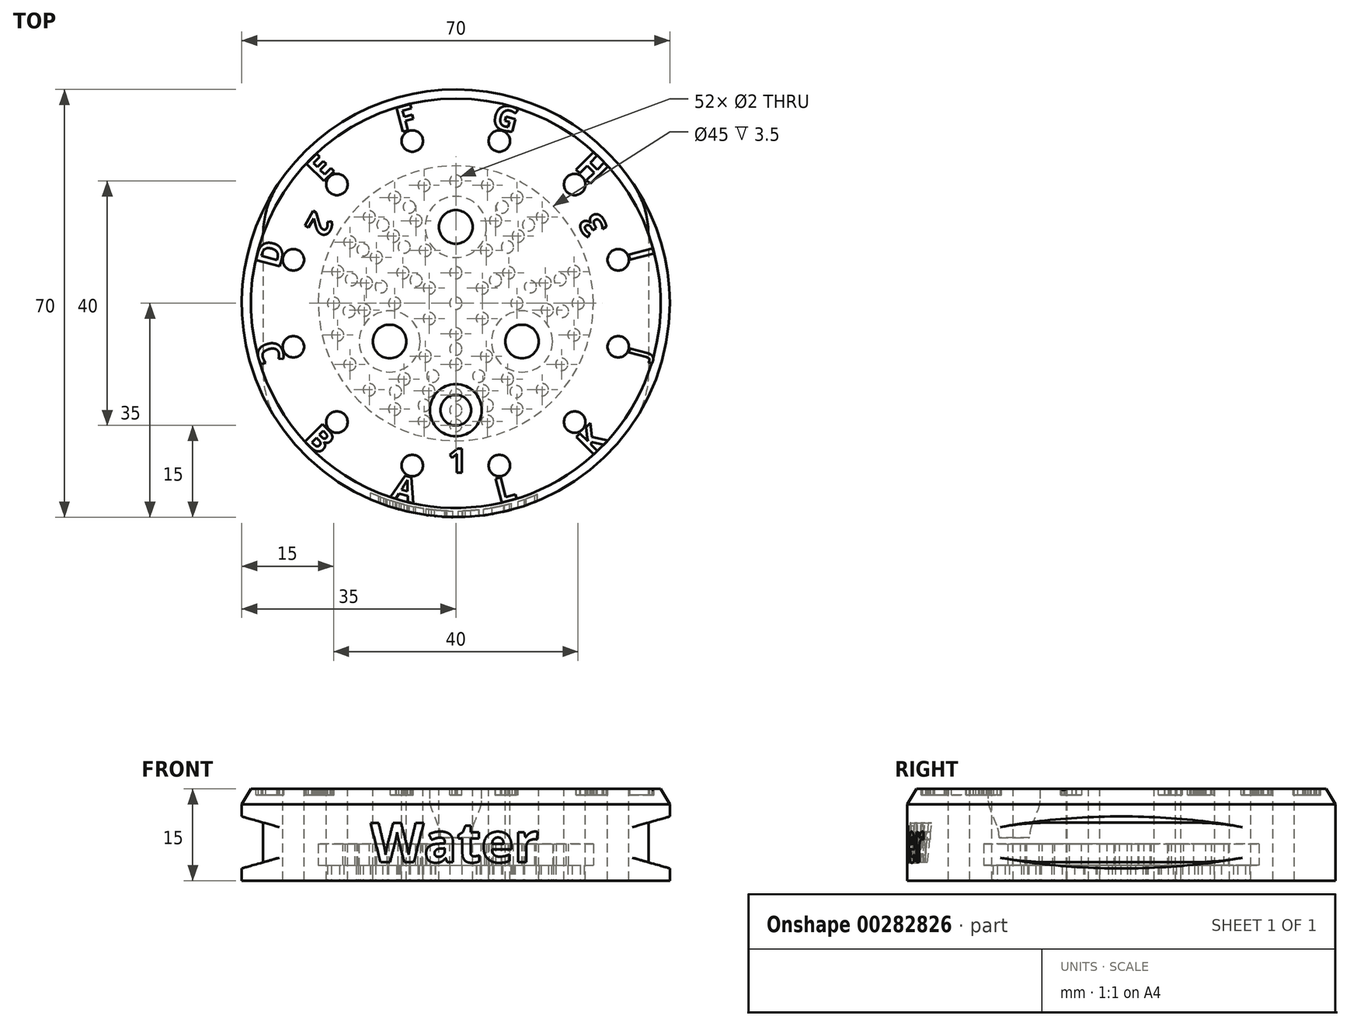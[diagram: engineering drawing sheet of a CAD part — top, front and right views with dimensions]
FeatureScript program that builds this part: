
annotation { "Feature Type Name" : "Feature", "Feature Type Description" : "" }
export const myFeature = defineFeature(function(context is Context, id is Id, definition is map)
    precondition{}
    {
        {
            var Q0;
            Q0=qCreatedBy(makeId("Top.planeOp"),FACE);
            var sketch = newSketch(context, id + "F0", { "sketchPlane" : qUnion([Q0])});
            skCircle(sketch, "E0", {"center": v(0, 0) * mm, "radius": 35 * mm});
            skSolve(sketch);
        }
        {
            var Q0;
            Q0=qSketchRegion(id+"F0",true);
            extrude(context, id + "F1", {"entities" : qUnion([Q0]), "depth" : 15 * mm});
        }
        {
            var Q0;
            Q0=qCreatedBy(makeId("Front.planeOp"),FACE);
            var sketch = newSketch(context, id + "F2", { "sketchPlane" : qUnion([Q0])});
            skText(sketch, "E1", { "text": "Water", "fontName": "OpenSans-Bold.ttf"});
            const initialGuessF2  = {"E1": [-0.01396, 0.003, 1, 0, 0.0065]};
            skSetInitialGuess(sketch, initialGuessF2);
            skSolve(sketch);
        }
        {
            var Q0;
            Q0=qSketchRegion(id+"F2",true);
            var Q1;
            Q1=makeQuery(id+"F1.opExtrude","SWEPT_FACE",FACE,{"disambiguationData":[OSD([sQuery(id+"F0.wireOp",EDGE,"E0")])]});
            extrude(context, id + "F3", {"entities" : qUnion([Q0]), "operationType" : NewBodyOperationType.REMOVE, "endBound" : BoundingType.THROUGH_ALL, "endBoundEntityFace" : qUnion([Q1]), "depth" : 25 * mm});
        }
        {
            var Q0;
            Q0=makeQuery(id+"F1.opExtrude","CAP_FACE",FACE,{"disambiguationData":[OSD([sQuery(id+"F0.wireOp",EDGE,"E0")])],"isStart":false});
            var sketch = newSketch(context, id + "F4", { "sketchPlane" : qUnion([Q0])});
            skCircle(sketch, "E2", {"center": v(0, 0) * mm, "radius": 34 * mm});
            skSolve(sketch);
        }
        {
            var Q0;
            Q0=qSketchRegion(id+"F4",true);
            var Q1;
            Q1=makeQuery(id+"F1.opExtrude","CAP_FACE",FACE,{"disambiguationData":[OSD([sQuery(id+"F0.wireOp",EDGE,"E0")])],"isStart":true});
            extrude(context, id + "F5", {"entities" : qUnion([Q0]), "operationType" : NewBodyOperationType.ADD, "endBound" : BoundingType.UP_TO_SURFACE, "oppositeDirection" : true, "endBoundEntityFace" : qUnion([Q1]), "depth" : 25 * mm});
        }
        {
            var Q0;
            Q0=qCreatedBy(makeId("Front.planeOp"),FACE);
            var sketch = newSketch(context, id + "F6", { "sketchPlane" : qUnion([Q0])});
            skLineSegment(sketch, "E3", {"start": v(-35, 10.5) * mm, "end": v(-35, 2) * mm});
            skLineSegment(sketch, "E4", {"start": v(-35, 2) * mm, "end": v(-31.5, 3) * mm});
            skLineSegment(sketch, "E5", {"start": v(-31.5, 3) * mm, "end": v(-31.5, 9.5) * mm});
            skLineSegment(sketch, "E6", {"start": v(-31.5, 9.5) * mm, "end": v(-35, 10.5) * mm});
            skLineSegment(sketch, "E7.MirrorCS", {"start": v(35, 10.5) * mm, "end": v(35, 2) * mm});
            skLineSegment(sketch, "E8.MirrorCS", {"start": v(31.5, 9.5) * mm, "end": v(35, 10.5) * mm});
            skLineSegment(sketch, "E9.MirrorCS", {"start": v(35, 2) * mm, "end": v(31.5, 3) * mm});
            skLineSegment(sketch, "E10.MirrorCS", {"start": v(31.5, 3) * mm, "end": v(31.5, 9.5) * mm});
            skSolve(sketch);
        }
        {
            var Q0;
            Q0=qSketchRegion(id+"F6",true);
            extrude(context, id + "F7", {"entities" : qUnion([Q0]), "operationType" : NewBodyOperationType.REMOVE, "endBound" : BoundingType.THROUGH_ALL, "oppositeDirection" : true, "depth" : 25 * mm, "hasSecondDirection" : true, "secondDirectionBound" : SecondDirectionBoundingType.THROUGH_ALL, "secondDirectionOppositeDirection" : false, "secondDirectionDepth" : 25 * mm});
        }
        {
            var Q0;
            {var subQ0=sQuery(id+"F0.wireOp",EDGE,"E0");Q0=makeQuery(id+"F7.boolean.opBoolean","INTERSECT",EDGE,{"disambiguationData":[OD(0.0)],"derivedFrom":[makeQuery(id+"F3.boolean.opBoolean","SPLIT",FACE,{"disambiguationData":[TD([makeQuery(id+"F1.opExtrude","CAP_FACE",FACE,{"disambiguationData":[OSD([subQ0])],"isStart":true})])],"derivedFrom":makeQuery(id+"F1.opExtrude","SWEPT_FACE",FACE,{"disambiguationData":[OSD([subQ0])]})}),makeQuery(id+"F7.opExtrude","SWEPT_FACE",FACE,{"disambiguationData":[OSD([sQuery(id+"F6.wireOp",EDGE,"E5")])]})]});}
            var Q1;
            {var subQ0=sQuery(id+"F0.wireOp",EDGE,"E0");Q1=makeQuery(id+"F7.boolean.opBoolean","INTERSECT",EDGE,{"disambiguationData":[OD(0.0)],"derivedFrom":[makeQuery(id+"F3.boolean.opBoolean","SPLIT",FACE,{"disambiguationData":[TD([makeQuery(id+"F1.opExtrude","CAP_FACE",FACE,{"disambiguationData":[OSD([subQ0])],"isStart":true})])],"derivedFrom":makeQuery(id+"F1.opExtrude","SWEPT_FACE",FACE,{"disambiguationData":[OSD([subQ0])]})}),makeQuery(id+"F7.opExtrude","SWEPT_FACE",FACE,{"disambiguationData":[OSD([sQuery(id+"F6.wireOp",EDGE,"E10.MirrorCS")])]})]});}
            var Q2;
            {var subQ0=sQuery(id+"F0.wireOp",EDGE,"E0");Q2=makeQuery(id+"F7.boolean.opBoolean","INTERSECT",EDGE,{"disambiguationData":[OD(1.0)],"derivedFrom":[makeQuery(id+"F3.boolean.opBoolean","SPLIT",FACE,{"disambiguationData":[TD([makeQuery(id+"F1.opExtrude","CAP_FACE",FACE,{"disambiguationData":[OSD([subQ0])],"isStart":true})])],"derivedFrom":makeQuery(id+"F1.opExtrude","SWEPT_FACE",FACE,{"disambiguationData":[OSD([subQ0])]})}),makeQuery(id+"F7.opExtrude","SWEPT_FACE",FACE,{"disambiguationData":[OSD([sQuery(id+"F6.wireOp",EDGE,"E10.MirrorCS")])]})]});}
            var Q3;
            {var subQ0=sQuery(id+"F0.wireOp",EDGE,"E0");Q3=makeQuery(id+"F7.boolean.opBoolean","INTERSECT",EDGE,{"disambiguationData":[OD(1.0)],"derivedFrom":[makeQuery(id+"F3.boolean.opBoolean","SPLIT",FACE,{"disambiguationData":[TD([makeQuery(id+"F1.opExtrude","CAP_FACE",FACE,{"disambiguationData":[OSD([subQ0])],"isStart":true})])],"derivedFrom":makeQuery(id+"F1.opExtrude","SWEPT_FACE",FACE,{"disambiguationData":[OSD([subQ0])]})}),makeQuery(id+"F7.opExtrude","SWEPT_FACE",FACE,{"disambiguationData":[OSD([sQuery(id+"F6.wireOp",EDGE,"E5")])]})]});}
            fillet(context, id + "F8", {"entities" : qUnion([Q0, Q1, Q2, Q3]), "radius" : 15 * mm, "tangentPropagation" : true, "allowEdgeOverflow" : false});
        }
        {
            var Q0;
            Q0=makeQuery(id+"F1.opExtrude","CAP_FACE",FACE,{"disambiguationData":[OSD([sQuery(id+"F0.wireOp",EDGE,"E0")])],"isStart":false});
            var sketch = newSketch(context, id + "F9", { "sketchPlane" : qUnion([Q0])});
            skCircle(sketch, "E11", {"center": v(0, 12.5) * mm, "radius": 2.75 * mm});
            skCircle(sketch, "E12.1.0", {"center": v(-10.83, -6.25) * mm, "radius": 2.75 * mm});
            skCircle(sketch, "E12.2.0", {"center": v(10.83, -6.25) * mm, "radius": 2.75 * mm});
            skPoint(sketch, "E12.center", {"position": v(0, 0) * mm});
            skCircle(sketch, "E13", {"center": v(0, 0) * mm, "radius": 12.5 * mm, "construction": true});
            skSolve(sketch);
        }
        {
            var Q0;
            Q0=qSketchRegion(id+"F9",true);
            extrude(context, id + "F10", {"entities" : qUnion([Q0]), "operationType" : NewBodyOperationType.REMOVE, "endBound" : BoundingType.THROUGH_ALL, "oppositeDirection" : true, "depth" : 25 * mm});
        }
        {
            var Q0;
            Q0=makeQuery(id+"F1.opExtrude","CAP_FACE",FACE,{"disambiguationData":[OSD([sQuery(id+"F0.wireOp",EDGE,"E0")])],"isStart":false});
            var sketch = newSketch(context, id + "F11", { "sketchPlane" : qUnion([Q0])});
            skCircle(sketch, "E14", {"center": v(0, -17.5) * mm, "radius": 2.5 * mm});
            skCircle(sketch, "E15", {"center": v(0, 0) * mm, "radius": 17.5 * mm, "construction": true});
            skSolve(sketch);
        }
        {
            var Q0;
            Q0=qSketchRegion(id+"F11",true);
            extrude(context, id + "F12", {"entities" : qUnion([Q0]), "operationType" : NewBodyOperationType.REMOVE, "endBound" : BoundingType.THROUGH_ALL, "oppositeDirection" : true, "depth" : 25 * mm});
        }
        {
            var Q0;
            Q0=makeQuery(id+"F1.opExtrude","CAP_FACE",FACE,{"disambiguationData":[OSD([sQuery(id+"F0.wireOp",EDGE,"E0")])],"isStart":false});
            var sketch = newSketch(context, id + "F13", { "sketchPlane" : qUnion([Q0])});
            skCircle(sketch, "E16", {"center": v(0, -17.5) * mm, "radius": 4.25 * mm});
            skSolve(sketch);
        }
        {
            var Q0;
            Q0=qSketchRegion(id+"F13",true);
            extrude(context, id + "F14", {"entities" : qUnion([Q0]), "operationType" : NewBodyOperationType.REMOVE, "oppositeDirection" : true, "depth" : 7.5 * mm});
        }
        {
            var Q0;
            Q0=makeQuery(id+"F14.boolean.opBoolean","COPY",EDGE,{"derivedFrom":makeQuery(id+"F14.opExtrude","CAP_EDGE",EDGE,{"disambiguationData":[OSD([sQuery(id+"F13.wireOp",EDGE,"E16")])],"isStart":false})});
            chamfer(context, id + "F15", {"entities" : qUnion([Q0]), "chamferType" : ChamferType.TWO_OFFSETS, "width1" : 5 * mm, "oppositeDirection" : true, "width2" : 2 * mm, "tangentPropagation" : true});
        }
        {
            var Q0;
            {var subQ0=sQuery(id+"F13.wireOp",EDGE,"E16");Q0=makeQuery(id+"F15.opChamfer","BLEND_EDGE",EDGE,{"blendedFrom":[makeQuery(id+"F14.boolean.opBoolean","COPY",EDGE,{"derivedFrom":makeQuery(id+"F14.opExtrude","CAP_EDGE",EDGE,{"disambiguationData":[OSD([subQ0])],"isStart":false})}),makeQuery(id+"F14.boolean.opBoolean","COPY",FACE,{"derivedFrom":makeQuery(id+"F14.opExtrude","SWEPT_FACE",FACE,{"disambiguationData":[OSD([subQ0])]})})],"blendedInto":[makeQuery(id+"F14.boolean.opBoolean","COPY",FACE,{"derivedFrom":makeQuery(id+"F14.opExtrude","SWEPT_FACE",FACE,{"disambiguationData":[OSD([subQ0])]})})]});}
            var Q1;
            Q1=makeQuery(id+"F15.opChamfer","BLEND_EDGE",EDGE,{"blendedFrom":[makeQuery(id+"F14.boolean.opBoolean","COPY",EDGE,{"derivedFrom":makeQuery(id+"F14.opExtrude","CAP_EDGE",EDGE,{"disambiguationData":[OSD([sQuery(id+"F13.wireOp",EDGE,"E16")])],"isStart":false})}),makeQuery(id+"F12.boolean.opBoolean","COPY",FACE,{"derivedFrom":makeQuery(id+"F12.opExtrude","SWEPT_FACE",FACE,{"disambiguationData":[OSD([sQuery(id+"F11.wireOp",EDGE,"E14")])]})})],"blendedInto":[makeQuery(id+"F12.boolean.opBoolean","COPY",FACE,{"derivedFrom":makeQuery(id+"F12.opExtrude","SWEPT_FACE",FACE,{"disambiguationData":[OSD([sQuery(id+"F11.wireOp",EDGE,"E14")])]})})]});
            fillet(context, id + "F16", {"entities" : qUnion([Q0, Q1]), "radius" : 5 * mm, "tangentPropagation" : true, "allowEdgeOverflow" : false});
        }
        {
            var Q0;
            Q0=makeQuery(id+"F1.opExtrude","CAP_FACE",FACE,{"disambiguationData":[OSD([sQuery(id+"F0.wireOp",EDGE,"E0")])],"isStart":false});
            var sketch = newSketch(context, id + "F17", { "sketchPlane" : qUnion([Q0])});
            skCircle(sketch, "E17", {"center": v(19.45, 19.45) * mm, "radius": 1.75 * mm});
            skCircle(sketch, "E18", {"center": v(0, 0) * mm, "radius": 27.5 * mm, "construction": true});
            skLineSegment(sketch, "E19", {"start": v(0, 0) * mm, "end": v(19.45, 19.45) * mm, "construction": true});
            skCircle(sketch, "E20.1.1", {"center": v(7.12, 26.56) * mm, "radius": 1.75 * mm});
            skCircle(sketch, "E20.2.1", {"center": v(-7.12, 26.56) * mm, "radius": 1.75 * mm});
            skCircle(sketch, "E20.3.1", {"center": v(-19.45, 19.45) * mm, "radius": 1.75 * mm});
            skCircle(sketch, "E20.4.1", {"center": v(-26.56, 7.12) * mm, "radius": 1.75 * mm});
            skCircle(sketch, "E20.5.1", {"center": v(-26.56, -7.12) * mm, "radius": 1.75 * mm});
            skCircle(sketch, "E20.6.1", {"center": v(-19.45, -19.45) * mm, "radius": 1.75 * mm});
            skCircle(sketch, "E20.7.1", {"center": v(-7.12, -26.56) * mm, "radius": 1.75 * mm});
            skCircle(sketch, "E20.8.1", {"center": v(7.12, -26.56) * mm, "radius": 1.75 * mm});
            skCircle(sketch, "E20.9.1", {"center": v(19.45, -19.45) * mm, "radius": 1.75 * mm});
            skCircle(sketch, "E20.10.1", {"center": v(26.56, -7.12) * mm, "radius": 1.75 * mm});
            skCircle(sketch, "E20.11.1", {"center": v(26.56, 7.12) * mm, "radius": 1.75 * mm});
            skSolve(sketch);
        }
        {
            var Q0;
            Q0=qSketchRegion(id+"F17",true);
            extrude(context, id + "F18", {"entities" : qUnion([Q0]), "operationType" : NewBodyOperationType.REMOVE, "endBound" : BoundingType.THROUGH_ALL, "oppositeDirection" : true, "depth" : 25 * mm});
        }
        {
            var Q0;
            Q0=makeQuery(id+"F1.opExtrude","CAP_EDGE",EDGE,{"disambiguationData":[OSD([sQuery(id+"F0.wireOp",EDGE,"E0")])],"isStart":false});
            chamfer(context, id + "F19", {"entities" : qUnion([Q0]), "chamferType" : ChamferType.TWO_OFFSETS, "width1" : 2.5 * mm, "oppositeDirection" : true, "width2" : 1.5 * mm, "tangentPropagation" : true});
        }
        {
            var Q0;
            Q0=makeQuery(id+"F1.opExtrude","CAP_FACE",FACE,{"disambiguationData":[OSD([sQuery(id+"F0.wireOp",EDGE,"E0")])],"isStart":false});
            var sketch = newSketch(context, id + "F20", { "sketchPlane" : qUnion([Q0])});
            skText(sketch, "E21", { "text": "A", "fontName": "OpenSans-Bold.ttf"});
            skText(sketch, "E22", { "text": "B", "fontName": "OpenSans-Bold.ttf"});
            skText(sketch, "E23", { "text": "C", "fontName": "OpenSans-Bold.ttf"});
            skText(sketch, "E24", { "text": "E", "fontName": "OpenSans-Bold.ttf"});
            skText(sketch, "E25", { "text": "F", "fontName": "OpenSans-Bold.ttf"});
            skText(sketch, "E26", { "text": "G", "fontName": "OpenSans-Bold.ttf"});
            skText(sketch, "E27", { "text": "H", "fontName": "OpenSans-Bold.ttf"});
            skText(sketch, "E28", { "text": "I", "fontName": "OpenSans-Bold.ttf"});
            skText(sketch, "E29", { "text": "J", "fontName": "OpenSans-Bold.ttf"});
            skText(sketch, "E30", { "text": "K", "fontName": "OpenSans-Bold.ttf"});
            skText(sketch, "E31", { "text": "L", "fontName": "OpenSans-Bold.ttf"});
            skText(sketch, "E32", { "text": "D", "fontName": "OpenSans-Bold.ttf"});
            skCircle(sketch, "E33", {"center": v(0, 0) * mm, "radius": 29.38 * mm, "construction": true});
            skText(sketch, "E34", { "text": "1", "fontName": "OpenSans-Bold.ttf"});
            skText(sketch, "E35", { "text": "2", "fontName": "OpenSans-Bold.ttf"});
            skText(sketch, "E36", { "text": "3", "fontName": "OpenSans-Bold.ttf"});
            skCircle(sketch, "E37", {"center": v(0, 0) * mm, "radius": 23.75 * mm, "construction": true});
            const initialGuessF20  = {"E21": [-0.0107, -0.03174, 0.96593, -0.25882, 0.00406], "E22": [-0.025, -0.02228, 0.7071, -0.7071, 0.00406], "E23": [-0.03278, -0.00684, 0.25882, -0.96593, 0.00406], "E24": [-0.0219, 0.01964, 0.7071, 0.7071, 0.00406], "E25": [-0.00914, 0.02796, 0.96593, 0.25882, 0.00406], "E26": [0.00567, 0.0289, 0.96593, -0.25882, 0.00406], "E27": [0.0193, 0.02225, 0.7071, -0.7071, 0.00406], "E28": [0.02815, 0.00844, 0.25882, -0.96593, 0.00406], "E29": [0.0313, -0.00927, 0.25882, 0.96593, 0.00325], "E30": [0.02219, -0.0251, 0.7071, 0.7071, 0.00406], "E31": [0.00703, -0.03273, 0.96593, 0.25882, 0.00406], "E32": [-0.02892, 0.00557, 0.25882, 0.96593, 0.00406], "E34": [-0.00133, -0.02775, 1, 0, 0.004], "E35": [-0.0232, 0.01533, -0.5, -0.86603, 0.004], "E36": [0.02486, 0.01244, -0.5, 0.86603, 0.004]};
            skSetInitialGuess(sketch, initialGuessF20);
            skSolve(sketch);
        }
        {
            var Q0;
            Q0=qSketchRegion(id+"F20",true);
            extrude(context, id + "F21", {"entities" : qUnion([Q0]), "operationType" : NewBodyOperationType.REMOVE, "oppositeDirection" : true, "depth" : 1 * mm});
        }
        {
            var Q0;
            Q0=makeQuery(id+"F1.opExtrude","CAP_FACE",FACE,{"disambiguationData":[OSD([sQuery(id+"F0.wireOp",EDGE,"E0")])],"isStart":true});
            var sketch = newSketch(context, id + "F22", { "sketchPlane" : qUnion([Q0])});
            skCircle(sketch, "E38.0", {"center": v(0, 17.5) * mm, "radius": 2.5 * mm});
            skCircle(sketch, "E38.1", {"center": v(-15.16, -8.75) * mm, "radius": 2.5 * mm});
            skSolve(sketch);
        }
        {
            var Q0;
            Q0=qSketchRegion(id+"F22",true);
            extrude(context, id + "F23", {"entities" : qUnion([Q0]), "operationType" : NewBodyOperationType.ADD, "oppositeDirection" : true, "depth" : 7 * mm});
        }
        {
            var Q0;
            Q0=makeQuery(id+"F23.boolean.opBoolean","MERGE",FACE,{"derivedFrom":[makeQuery(id+"F1.opExtrude","CAP_FACE",FACE,{"disambiguationData":[OSD([sQuery(id+"F0.wireOp",EDGE,"E0")])],"isStart":true}),makeQuery(id+"F23.opExtrude","CAP_FACE",FACE,{"disambiguationData":[OSD([sQuery(id+"F22.wireOp",EDGE,"E38.0")])],"isStart":true}),makeQuery(id+"F23.opExtrude","CAP_FACE",FACE,{"disambiguationData":[OSD([sQuery(id+"F22.wireOp",EDGE,"E38.1")])],"isStart":true})]});
            var sketch = newSketch(context, id + "F24", { "sketchPlane" : qUnion([Q0])});
            skCircle(sketch, "E39", {"center": v(0, 0) * mm, "radius": 22.5 * mm});
            skCircle(sketch, "E40", {"center": v(10.83, 6.25) * mm, "radius": 5 * mm});
            skCircle(sketch, "E41", {"center": v(-10.83, 6.25) * mm, "radius": 5 * mm});
            skCircle(sketch, "E42", {"center": v(0, -12.5) * mm, "radius": 5 * mm});
            skSolve(sketch);
        }
        {
            var Q0;
            Q0=qSketchRegion(id+"F24",true);
            extrude(context, id + "F25", {"entities" : qUnion([Q0]), "operationType" : NewBodyOperationType.REMOVE, "oppositeDirection" : true, "depth" : 6 * mm});
        }
        {
            var Q0;
            Q0=makeQuery(id+"F25.boolean.opBoolean","COPY",FACE,{"derivedFrom":makeQuery(id+"F25.opExtrude","CAP_FACE",FACE,{"disambiguationData":[OSD([sQuery(id+"F24.wireOp",EDGE,"E39"),sQuery(id+"F24.wireOp",EDGE,"E40"),sQuery(id+"F24.wireOp",EDGE,"E41"),sQuery(id+"F24.wireOp",EDGE,"E42")])],"isStart":false})});
            var sketch = newSketch(context, id + "F26", { "sketchPlane" : qUnion([Q0])});
            skCircle(sketch, "E43", {"center": v(0, 0) * mm, "radius": 1 * mm});
            skCircle(sketch, "E44", {"center": v(0, 7.5) * mm, "radius": 1 * mm});
            skCircle(sketch, "E45", {"center": v(3.76, 11.92) * mm, "radius": 1 * mm});
            skCircle(sketch, "E46", {"center": v(-3.76, 11.92) * mm, "radius": 1 * mm});
            skCircle(sketch, "E47", {"center": v(0, 17.5) * mm, "radius": 1 * mm});
            skLineSegment(sketch, "E48", {"start": v(3.76, 11.92) * mm, "end": v(0, 0) * mm, "construction": true});
            skCircle(sketch, "E49.1.0", {"center": v(-6.5, -3.75) * mm, "radius": 1 * mm});
            skCircle(sketch, "E49.1.1", {"center": v(-8.44, -9.22) * mm, "radius": 1 * mm});
            skCircle(sketch, "E49.1.2", {"center": v(-12.2, -2.7) * mm, "radius": 1 * mm});
            skCircle(sketch, "E49.2.0", {"center": v(6.5, -3.75) * mm, "radius": 1 * mm});
            skCircle(sketch, "E49.2.1", {"center": v(12.2, -2.7) * mm, "radius": 1 * mm});
            skCircle(sketch, "E49.2.2", {"center": v(8.44, -9.22) * mm, "radius": 1 * mm});
            skCircle(sketch, "E50.1.0", {"center": v(-5.16, 16.72) * mm, "radius": 1 * mm});
            skCircle(sketch, "E50.2.0", {"center": v(-9.86, 14.46) * mm, "radius": 1 * mm});
            skCircle(sketch, "E50.5.0", {"center": v(-17.45, 1.3) * mm, "radius": 1 * mm});
            skCircle(sketch, "E50.6.0", {"center": v(-17.06, -3.9) * mm, "radius": 1 * mm});
            skCircle(sketch, "E50.7.0", {"center": v(-15.16, -8.75) * mm, "radius": 1 * mm});
            skCircle(sketch, "E50.8.0", {"center": v(-11.9, -12.83) * mm, "radius": 1 * mm});
            skCircle(sketch, "E50.9.0", {"center": v(-7.6, -15.77) * mm, "radius": 1 * mm});
            skCircle(sketch, "E50.12.0", {"center": v(7.6, -15.77) * mm, "radius": 1 * mm});
            skCircle(sketch, "E50.13.0", {"center": v(11.9, -12.83) * mm, "radius": 1 * mm});
            skCircle(sketch, "E50.15.0", {"center": v(17.06, -3.9) * mm, "radius": 1 * mm});
            skCircle(sketch, "E50.16.0", {"center": v(17.45, 1.3) * mm, "radius": 1 * mm});
            skCircle(sketch, "E50.19.0", {"center": v(9.86, 14.46) * mm, "radius": 1 * mm});
            skCircle(sketch, "E50.20.0", {"center": v(5.16, 16.72) * mm, "radius": 1 * mm});
            skSolve(sketch);
        }
        {
            var Q0;
            Q0=qSketchRegion(id+"F26",true);
            var Q1;
            {var subQ0=sQuery(id+"F0.wireOp",EDGE,"E0");Q1=makeQuery(id+"F25.boolean.opBoolean","SPLIT",FACE,{"disambiguationData":[TD([makeQuery(id+"F1.opExtrude","SWEPT_FACE",FACE,{"disambiguationData":[OSD([subQ0])]})])],"derivedFrom":makeQuery(id+"F23.boolean.opBoolean","MERGE",FACE,{"derivedFrom":[makeQuery(id+"F1.opExtrude","CAP_FACE",FACE,{"disambiguationData":[OSD([subQ0])],"isStart":true}),makeQuery(id+"F23.opExtrude","CAP_FACE",FACE,{"disambiguationData":[OSD([sQuery(id+"F22.wireOp",EDGE,"E38.0")])],"isStart":true}),makeQuery(id+"F23.opExtrude","CAP_FACE",FACE,{"disambiguationData":[OSD([sQuery(id+"F22.wireOp",EDGE,"E38.1")])],"isStart":true})]})});}
            extrude(context, id + "F27", {"entities" : qUnion([Q0]), "operationType" : NewBodyOperationType.ADD, "endBound" : BoundingType.UP_TO_SURFACE, "endBoundEntityFace" : qUnion([Q1]), "depth" : 25 * mm});
        }
        {
            var Q0;
            {var subQ0=sQuery(id+"F0.wireOp",EDGE,"E0");Q0=makeQuery(id+"F25.boolean.opBoolean","SPLIT",FACE,{"disambiguationData":[TD([makeQuery(id+"F1.opExtrude","SWEPT_FACE",FACE,{"disambiguationData":[OSD([subQ0])]})])],"derivedFrom":makeQuery(id+"F23.boolean.opBoolean","MERGE",FACE,{"derivedFrom":[makeQuery(id+"F1.opExtrude","CAP_FACE",FACE,{"disambiguationData":[OSD([subQ0])],"isStart":true}),makeQuery(id+"F23.opExtrude","CAP_FACE",FACE,{"disambiguationData":[OSD([sQuery(id+"F22.wireOp",EDGE,"E38.0")])],"isStart":true}),makeQuery(id+"F23.opExtrude","CAP_FACE",FACE,{"disambiguationData":[OSD([sQuery(id+"F22.wireOp",EDGE,"E38.1")])],"isStart":true})]})});}
            var sketch = newSketch(context, id + "F28", { "sketchPlane" : qUnion([Q0])});
            skCircle(sketch, "E51.0", {"center": v(0, 0) * mm, "radius": 22.5 * mm});
            skCircle(sketch, "E52.0", {"center": v(-10.83, 6.25) * mm, "radius": 2.75 * mm});
            skCircle(sketch, "E52.1", {"center": v(10.83, 6.25) * mm, "radius": 2.75 * mm});
            skCircle(sketch, "E52.2", {"center": v(0, -12.5) * mm, "radius": 2.75 * mm});
            skSolve(sketch);
        }
        {
            var Q0;
            Q0=qSketchRegion(id+"F28",true);
            extrude(context, id + "F29", {"entities" : qUnion([Q0]), "operationType" : NewBodyOperationType.ADD, "oppositeDirection" : true, "depth" : 2.5 * mm});
        }
        {
            var Q0;
            {var subQ0=sQuery(id+"F0.wireOp",EDGE,"E0");var subQ1=makeQuery(id+"F23.boolean.opBoolean","MERGE",FACE,{"derivedFrom":[makeQuery(id+"F1.opExtrude","CAP_FACE",FACE,{"disambiguationData":[OSD([subQ0])],"isStart":true}),makeQuery(id+"F23.opExtrude","CAP_FACE",FACE,{"disambiguationData":[OSD([sQuery(id+"F22.wireOp",EDGE,"E38.0")])],"isStart":true}),makeQuery(id+"F23.opExtrude","CAP_FACE",FACE,{"disambiguationData":[OSD([sQuery(id+"F22.wireOp",EDGE,"E38.1")])],"isStart":true})]});Q0=makeQuery(id+"F29.boolean.opBoolean","MERGE",FACE,{"derivedFrom":[makeQuery(id+"F25.boolean.opBoolean","SPLIT",FACE,{"disambiguationData":[TD([makeQuery(id+"F1.opExtrude","SWEPT_FACE",FACE,{"disambiguationData":[OSD([subQ0])]})])],"derivedFrom":subQ1}),makeQuery(id+"F25.boolean.opBoolean","SPLIT",FACE,{"disambiguationData":[TD([makeQuery(id+"F10.boolean.opBoolean","COPY",FACE,{"derivedFrom":makeQuery(id+"F10.opExtrude","SWEPT_FACE",FACE,{"disambiguationData":[OSD([sQuery(id+"F9.wireOp",EDGE,"E11")])]})})])],"derivedFrom":subQ1}),makeQuery(id+"F25.boolean.opBoolean","SPLIT",FACE,{"disambiguationData":[TD([makeQuery(id+"F10.boolean.opBoolean","COPY",FACE,{"derivedFrom":makeQuery(id+"F10.opExtrude","SWEPT_FACE",FACE,{"disambiguationData":[OSD([sQuery(id+"F9.wireOp",EDGE,"E12.1.0")])]})})])],"derivedFrom":subQ1}),makeQuery(id+"F25.boolean.opBoolean","SPLIT",FACE,{"disambiguationData":[TD([makeQuery(id+"F10.boolean.opBoolean","COPY",FACE,{"derivedFrom":makeQuery(id+"F10.opExtrude","SWEPT_FACE",FACE,{"disambiguationData":[OSD([sQuery(id+"F9.wireOp",EDGE,"E12.2.0")])]})})])],"derivedFrom":subQ1}),makeQuery(id+"F27.opExtrude","CAP_FACE",FACE,{"disambiguationData":[OSD([sQuery(id+"F26.wireOp",EDGE,"E43")])],"isStart":false}),makeQuery(id+"F27.opExtrude","CAP_FACE",FACE,{"disambiguationData":[OSD([sQuery(id+"F26.wireOp",EDGE,"E44")])],"isStart":false}),makeQuery(id+"F27.opExtrude","CAP_FACE",FACE,{"disambiguationData":[OSD([sQuery(id+"F26.wireOp",EDGE,"E45")])],"isStart":false}),makeQuery(id+"F27.opExtrude","CAP_FACE",FACE,{"disambiguationData":[OSD([sQuery(id+"F26.wireOp",EDGE,"E46")])],"isStart":false}),makeQuery(id+"F27.opExtrude","CAP_FACE",FACE,{"disambiguationData":[OSD([sQuery(id+"F26.wireOp",EDGE,"E47")])],"isStart":false}),makeQuery(id+"F27.opExtrude","CAP_FACE",FACE,{"disambiguationData":[OSD([sQuery(id+"F26.wireOp",EDGE,"E49.1.0")])],"isStart":false}),makeQuery(id+"F27.opExtrude","CAP_FACE",FACE,{"disambiguationData":[OSD([sQuery(id+"F26.wireOp",EDGE,"E49.1.1")])],"isStart":false}),makeQuery(id+"F27.opExtrude","CAP_FACE",FACE,{"disambiguationData":[OSD([sQuery(id+"F26.wireOp",EDGE,"E49.1.2")])],"isStart":false}),makeQuery(id+"F27.opExtrude","CAP_FACE",FACE,{"disambiguationData":[OSD([sQuery(id+"F26.wireOp",EDGE,"E49.2.0")])],"isStart":false}),makeQuery(id+"F27.opExtrude","CAP_FACE",FACE,{"disambiguationData":[OSD([sQuery(id+"F26.wireOp",EDGE,"E49.2.1")])],"isStart":false}),makeQuery(id+"F27.opExtrude","CAP_FACE",FACE,{"disambiguationData":[OSD([sQuery(id+"F26.wireOp",EDGE,"E49.2.2")])],"isStart":false}),makeQuery(id+"F27.opExtrude","CAP_FACE",FACE,{"disambiguationData":[OSD([sQuery(id+"F26.wireOp",EDGE,"E50.1.0")])],"isStart":false}),makeQuery(id+"F27.opExtrude","CAP_FACE",FACE,{"disambiguationData":[OSD([sQuery(id+"F26.wireOp",EDGE,"E50.2.0")])],"isStart":false}),makeQuery(id+"F27.opExtrude","CAP_FACE",FACE,{"disambiguationData":[OSD([sQuery(id+"F26.wireOp",EDGE,"E50.5.0")])],"isStart":false}),makeQuery(id+"F27.opExtrude","CAP_FACE",FACE,{"disambiguationData":[OSD([sQuery(id+"F26.wireOp",EDGE,"E50.6.0")])],"isStart":false}),makeQuery(id+"F27.opExtrude","CAP_FACE",FACE,{"disambiguationData":[OSD([sQuery(id+"F26.wireOp",EDGE,"E50.7.0")])],"isStart":false}),makeQuery(id+"F27.opExtrude","CAP_FACE",FACE,{"disambiguationData":[OSD([sQuery(id+"F26.wireOp",EDGE,"E50.8.0")])],"isStart":false}),makeQuery(id+"F27.opExtrude","CAP_FACE",FACE,{"disambiguationData":[OSD([sQuery(id+"F26.wireOp",EDGE,"E50.9.0")])],"isStart":false}),makeQuery(id+"F27.opExtrude","CAP_FACE",FACE,{"disambiguationData":[OSD([sQuery(id+"F26.wireOp",EDGE,"E50.12.0")])],"isStart":false}),makeQuery(id+"F27.opExtrude","CAP_FACE",FACE,{"disambiguationData":[OSD([sQuery(id+"F26.wireOp",EDGE,"E50.13.0")])],"isStart":false}),makeQuery(id+"F27.opExtrude","CAP_FACE",FACE,{"disambiguationData":[OSD([sQuery(id+"F26.wireOp",EDGE,"E50.15.0")])],"isStart":false}),makeQuery(id+"F27.opExtrude","CAP_FACE",FACE,{"disambiguationData":[OSD([sQuery(id+"F26.wireOp",EDGE,"E50.16.0")])],"isStart":false}),makeQuery(id+"F27.opExtrude","CAP_FACE",FACE,{"disambiguationData":[OSD([sQuery(id+"F26.wireOp",EDGE,"E50.19.0")])],"isStart":false}),makeQuery(id+"F27.opExtrude","CAP_FACE",FACE,{"disambiguationData":[OSD([sQuery(id+"F26.wireOp",EDGE,"E50.20.0")])],"isStart":false}),makeQuery(id+"F29.opExtrude","CAP_FACE",FACE,{"disambiguationData":[OSD([sQuery(id+"F28.wireOp",EDGE,"E51.0")])],"isStart":true})]});}
            var sketch = newSketch(context, id + "F30", { "sketchPlane" : qUnion([Q0])});
            skCircle(sketch, "E53", {"center": v(0, 5) * mm, "radius": 1 * mm});
            skCircle(sketch, "E54.0.1.0", {"center": v(0, 10) * mm, "radius": 1 * mm});
            skCircle(sketch, "E54.0.2.0", {"center": v(0, 15) * mm, "radius": 1 * mm});
            skCircle(sketch, "E54.0.3.0", {"center": v(0, 20) * mm, "radius": 1 * mm});
            skLineSegment(sketch, "E54.direction1", {"start": v(0, 5) * mm, "end": v(25, 5) * mm, "construction": true});
            skLineSegment(sketch, "E54.direction2", {"start": v(0, 5) * mm, "end": v(0, 10) * mm, "construction": true});
            skCircle(sketch, "E55.1.0", {"center": v(-4.33, 2.5) * mm, "radius": 1 * mm});
            skCircle(sketch, "E55.2.0", {"center": v(-4.33, -2.5) * mm, "radius": 1 * mm});
            skCircle(sketch, "E55.3.0", {"center": v(0, -5) * mm, "radius": 1 * mm});
            skCircle(sketch, "E55.4.0", {"center": v(4.33, -2.5) * mm, "radius": 1 * mm});
            skCircle(sketch, "E55.5.0", {"center": v(4.33, 2.5) * mm, "radius": 1 * mm});
            skPoint(sketch, "E55.center", {"position": v(0, 0) * mm});
            skCircle(sketch, "E56.1.0", {"center": v(-5, 8.66) * mm, "radius": 1 * mm});
            skCircle(sketch, "E56.3.0", {"center": v(-10, 0) * mm, "radius": 1 * mm});
            skCircle(sketch, "E56.4.0", {"center": v(-8.66, -5) * mm, "radius": 1 * mm});
            skCircle(sketch, "E56.5.0", {"center": v(-5, -8.66) * mm, "radius": 1 * mm});
            skCircle(sketch, "E56.7.0", {"center": v(5, -8.66) * mm, "radius": 1 * mm});
            skCircle(sketch, "E56.8.0", {"center": v(8.66, -5) * mm, "radius": 1 * mm});
            skCircle(sketch, "E56.9.0", {"center": v(10, 0) * mm, "radius": 1 * mm});
            skCircle(sketch, "E56.11.0", {"center": v(5, 8.66) * mm, "radius": 1 * mm});
            skCircle(sketch, "E57.1.0", {"center": v(-4.42, 14.33) * mm, "radius": 1 * mm});
            skCircle(sketch, "E57.2.0", {"center": v(-8.45, 12.4) * mm, "radius": 1 * mm});
            skCircle(sketch, "E57.5.0", {"center": v(-14.96, 1.12) * mm, "radius": 1 * mm});
            skCircle(sketch, "E57.6.0", {"center": v(-14.62, -3.34) * mm, "radius": 1 * mm});
            skCircle(sketch, "E57.7.0", {"center": v(-13, -7.5) * mm, "radius": 1 * mm});
            skCircle(sketch, "E57.8.0", {"center": v(-10.2, -11) * mm, "radius": 1 * mm});
            skCircle(sketch, "E57.9.0", {"center": v(-6.5, -13.51) * mm, "radius": 1 * mm});
            skCircle(sketch, "E57.12.0", {"center": v(6.5, -13.51) * mm, "radius": 1 * mm});
            skCircle(sketch, "E57.13.0", {"center": v(10.2, -11) * mm, "radius": 1 * mm});
            skCircle(sketch, "E57.15.0", {"center": v(14.62, -3.34) * mm, "radius": 1 * mm});
            skCircle(sketch, "E57.16.0", {"center": v(14.96, 1.12) * mm, "radius": 1 * mm});
            skCircle(sketch, "E57.19.0", {"center": v(8.45, 12.4) * mm, "radius": 1 * mm});
            skCircle(sketch, "E57.20.0", {"center": v(4.42, 14.33) * mm, "radius": 1 * mm});
            skCircle(sketch, "E58.1.0", {"center": v(-5.18, 19.32) * mm, "radius": 1 * mm});
            skCircle(sketch, "E58.2.0", {"center": v(-10, 17.32) * mm, "radius": 1 * mm});
            skCircle(sketch, "E58.3.0", {"center": v(-14.14, 14.14) * mm, "radius": 1 * mm});
            skCircle(sketch, "E58.4.0", {"center": v(-17.32, 10) * mm, "radius": 1 * mm});
            skCircle(sketch, "E58.5.0", {"center": v(-19.32, 5.18) * mm, "radius": 1 * mm});
            skCircle(sketch, "E58.6.0", {"center": v(-20, 0) * mm, "radius": 1 * mm});
            skCircle(sketch, "E58.7.0", {"center": v(-19.32, -5.18) * mm, "radius": 1 * mm});
            skCircle(sketch, "E58.8.0", {"center": v(-17.32, -10) * mm, "radius": 1 * mm});
            skCircle(sketch, "E58.9.0", {"center": v(-14.14, -14.14) * mm, "radius": 1 * mm});
            skCircle(sketch, "E58.10.0", {"center": v(-10, -17.32) * mm, "radius": 1 * mm});
            skCircle(sketch, "E58.11.0", {"center": v(-5.18, -19.32) * mm, "radius": 1 * mm});
            skCircle(sketch, "E58.12.0", {"center": v(0, -20) * mm, "radius": 1 * mm});
            skCircle(sketch, "E58.13.0", {"center": v(5.18, -19.32) * mm, "radius": 1 * mm});
            skCircle(sketch, "E58.14.0", {"center": v(10, -17.32) * mm, "radius": 1 * mm});
            skCircle(sketch, "E58.15.0", {"center": v(14.14, -14.14) * mm, "radius": 1 * mm});
            skCircle(sketch, "E58.17.0", {"center": v(19.32, -5.18) * mm, "radius": 1 * mm});
            skCircle(sketch, "E58.18.0", {"center": v(20, 0) * mm, "radius": 1 * mm});
            skCircle(sketch, "E58.19.0", {"center": v(19.32, 5.18) * mm, "radius": 1 * mm});
            skCircle(sketch, "E58.20.0", {"center": v(17.32, 10) * mm, "radius": 1 * mm});
            skCircle(sketch, "E58.21.0", {"center": v(14.14, 14.14) * mm, "radius": 1 * mm});
            skCircle(sketch, "E58.22.0", {"center": v(10, 17.32) * mm, "radius": 1 * mm});
            skCircle(sketch, "E58.23.0", {"center": v(5.18, 19.32) * mm, "radius": 1 * mm});
            skSolve(sketch);
        }
        {
            var Q0;
            Q0=qSketchRegion(id+"F30",true);
            extrude(context, id + "F31", {"entities" : qUnion([Q0]), "operationType" : NewBodyOperationType.REMOVE, "endBound" : BoundingType.UP_TO_NEXT, "oppositeDirection" : true, "depth" : 25 * mm});
        }
    });
